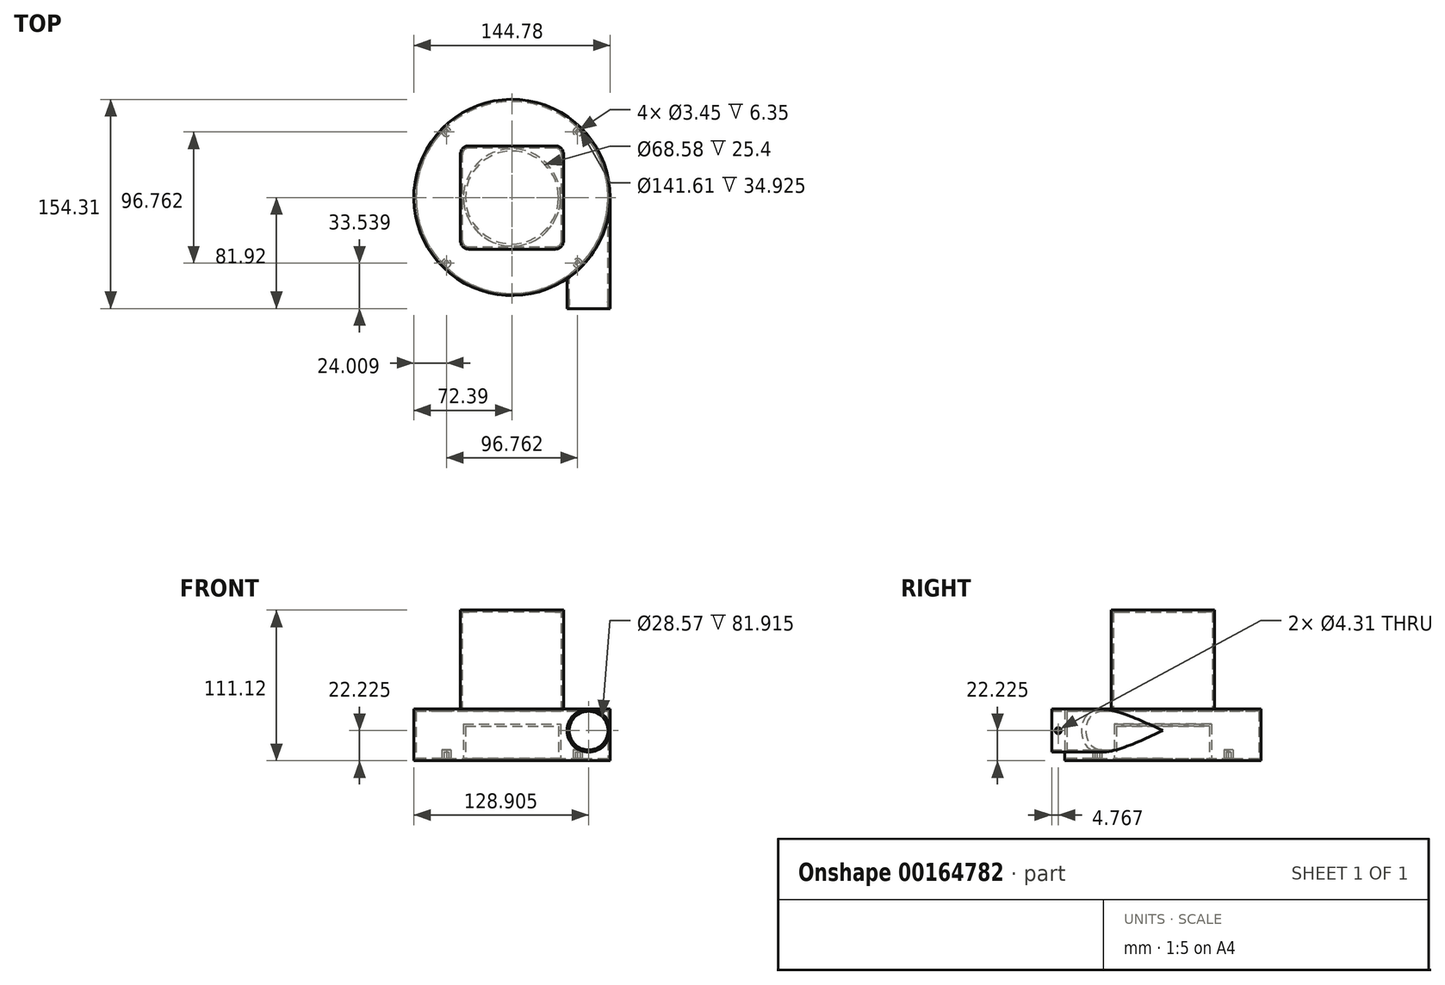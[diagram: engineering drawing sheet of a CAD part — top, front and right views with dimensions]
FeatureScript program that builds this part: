
annotation { "Feature Type Name" : "Feature", "Feature Type Description" : "" }
export const myFeature = defineFeature(function(context is Context, id is Id, definition is map)
    precondition{}
    {
        {
            var Q0;
            Q0=qCreatedBy(makeId("Top.planeOp"),FACE);
            var sketch = newSketch(context, id + "F0", { "sketchPlane" : qUnion([Q0])});
            skCircle(sketch, "E0", {"center": v(0, 0) * mm, "radius": 72.4 * mm});
            skSolve(sketch);
        }
        {
            var Q0;
            Q0=qSketchRegion(id+"F0",true);
            extrude(context, id + "F1", {"entities" : qUnion([Q0]), "depth" : 38.1 * mm});
        }
        {
            var Q0;
            Q0=makeQuery(id+"F1.opExtrude","CAP_FACE",FACE,{"disambiguationData":[OSD([sQuery(id+"F0.wireOp",EDGE,"E0")])],"isStart":false});
            var sketch = newSketch(context, id + "F2", { "sketchPlane" : qUnion([Q0])});
            skLineSegment(sketch, "E1.bottom", {"start": v(38.1, -38.1) * mm, "end": v(-38.1, -38.1) * mm});
            skLineSegment(sketch, "E1.top", {"start": v(38.1, 38.1) * mm, "end": v(-38.1, 38.1) * mm});
            skLineSegment(sketch, "E1.left", {"start": v(38.1, -38.1) * mm, "end": v(38.1, 38.1) * mm});
            skLineSegment(sketch, "E1.right", {"start": v(-38.1, -38.1) * mm, "end": v(-38.1, 38.1) * mm});
            skPoint(sketch, "E1.middle", {"position": v(0, 0) * mm});
            skSolve(sketch);
        }
        {
            var Q0;
            Q0=qSketchRegion(id+"F2",true);
            extrude(context, id + "F3", {"entities" : qUnion([Q0]), "operationType" : NewBodyOperationType.ADD, "depth" : 73.02 * mm});
        }
        {
            var Q0;
            Q0=makeQuery(id+"F3.opExtrude","SWEPT_EDGE",EDGE,{"disambiguationData":[OSD([sQuery(id+"F2.wireOp",EDGE,"E1.bottom"),sQuery(id+"F2.wireOp",EDGE,"E1.right")])]});
            var Q1;
            Q1=makeQuery(id+"F3.opExtrude","SWEPT_EDGE",EDGE,{"disambiguationData":[OSD([sQuery(id+"F2.wireOp",EDGE,"E1.top"),sQuery(id+"F2.wireOp",EDGE,"E1.right")])]});
            var Q2;
            Q2=makeQuery(id+"F3.opExtrude","SWEPT_EDGE",EDGE,{"disambiguationData":[OSD([sQuery(id+"F2.wireOp",EDGE,"E1.bottom"),sQuery(id+"F2.wireOp",EDGE,"E1.left")])]});
            var Q3;
            Q3=makeQuery(id+"F3.opExtrude","SWEPT_EDGE",EDGE,{"disambiguationData":[OSD([sQuery(id+"F2.wireOp",EDGE,"E1.top"),sQuery(id+"F2.wireOp",EDGE,"E1.left")])]});
            fillet(context, id + "F4", {"entities" : qUnion([Q0, Q1, Q2, Q3]), "radius" : 6.35 * mm, "tangentPropagation" : true, "allowEdgeOverflow" : false});
        }
        {
            var Q0;
            Q0=makeQuery(id+"F1.opExtrude","CAP_FACE",FACE,{"disambiguationData":[OSD([sQuery(id+"F0.wireOp",EDGE,"E0")])],"isStart":true});
            var sketch = newSketch(context, id + "F5", { "sketchPlane" : qUnion([Q0])});
            skLineSegment(sketch, "E2.bottom", {"start": v(48.38, 48.38) * mm, "end": v(-48.38, 48.38) * mm, "construction": true});
            skLineSegment(sketch, "E2.top", {"start": v(48.38, -48.38) * mm, "end": v(-48.38, -48.38) * mm, "construction": true});
            skLineSegment(sketch, "E2.left", {"start": v(48.38, 48.38) * mm, "end": v(48.38, -48.38) * mm, "construction": true});
            skLineSegment(sketch, "E2.right", {"start": v(-48.38, 48.38) * mm, "end": v(-48.38, -48.38) * mm, "construction": true});
            skPoint(sketch, "E2.middle", {"position": v(0, 0) * mm});
            skCircle(sketch, "E3", {"center": v(48.38, 48.38) * mm, "radius": 3.97 * mm, "construction": true});
            skCircle(sketch, "E4", {"center": v(-48.38, 48.38) * mm, "radius": 1.73 * mm});
            skCircle(sketch, "E5", {"center": v(-48.38, -48.38) * mm, "radius": 1.73 * mm});
            skCircle(sketch, "E6", {"center": v(48.38, -48.38) * mm, "radius": 1.73 * mm});
            skCircle(sketch, "E7", {"center": v(48.38, 48.38) * mm, "radius": 1.73 * mm});
            skSolve(sketch);
        }
        {
            var Q0;
            Q0=qSketchRegion(id+"F5",true);
            extrude(context, id + "F6", {"entities" : qUnion([Q0]), "operationType" : NewBodyOperationType.REMOVE, "oppositeDirection" : true, "depth" : 6.35 * mm});
        }
        {
            var Q0;
            Q0=makeQuery(id+"F1.opExtrude","CAP_FACE",FACE,{"disambiguationData":[OSD([sQuery(id+"F0.wireOp",EDGE,"E0")])],"isStart":true});
            var sketch = newSketch(context, id + "F7", { "sketchPlane" : qUnion([Q0])});
            skCircle(sketch, "E8", {"center": v(0, 0) * mm, "radius": 34.3 * mm});
            skSolve(sketch);
        }
        {
            var Q0;
            Q0=qSketchRegion(id+"F7",true);
            extrude(context, id + "F8", {"entities" : qUnion([Q0]), "operationType" : NewBodyOperationType.REMOVE, "oppositeDirection" : true, "depth" : 25.4 * mm});
        }
        {
            var Q0;
            Q0=qCreatedBy(makeId("Front.planeOp"),FACE);
            var sketch = newSketch(context, id + "F9", { "sketchPlane" : qUnion([Q0])});
            skCircle(sketch, "E9", {"center": v(56.52, 22.23) * mm, "radius": 15.88 * mm});
            skLineSegment(sketch, "E10.bottom", {"start": v(0, 0) * mm, "end": v(72.4, 0) * mm, "construction": true});
            skLineSegment(sketch, "E10.top", {"start": v(0, 38.1) * mm, "end": v(72.4, 38.1) * mm, "construction": true});
            skLineSegment(sketch, "E10.left", {"start": v(0, 0) * mm, "end": v(0, 38.1) * mm, "construction": true});
            skLineSegment(sketch, "E10.right", {"start": v(72.4, 0) * mm, "end": v(72.4, 38.1) * mm, "construction": true});
            skSolve(sketch);
        }
        {
            var Q0;
            Q0 = qSketchRegion(id + "F9", true);
            extrude(context, id + "F10", {"entities" : qUnion([Q0]), "operationType" : NewBodyOperationType.ADD, "depth" : 81.9 * mm});
        }
        {
            var Q0;
            Q0=makeQuery(id+"F10.opExtrude","CAP_FACE",FACE,{"disambiguationData":[OSD([sQuery(id+"F9.wireOp",EDGE,"E9")])],"isStart":false});
            shell(context, id + "F11", {"entities" : qUnion([Q0]), "thickness" : 1.59 * mm});
        }
        {
            var Q0;
            Q0=qCreatedBy(makeId("Right.planeOp"),FACE);
            var sketch = newSketch(context, id + "F12", { "sketchPlane" : qUnion([Q0])});
            skLineSegment(sketch, "E11", {"start": v(-81.92, 22.23) * mm, "end": v(-77.15, 22.23) * mm, "construction": true});
            skCircle(sketch, "E12", {"center": v(-77.15, 22.23) * mm, "radius": 2.15 * mm});
            skSolve(sketch);
        }
        {
            var Q0;
            Q0 = qSketchRegion(id + "F12", true);
            var Q1;
            Q1=makeQuery(id+"F10.opExtrude","SWEPT_FACE",FACE,{"disambiguationData":[OSD([sQuery(id+"F9.wireOp",EDGE,"E9")])]});
            extrude(context, id + "F13", {"entities" : qUnion([Q0]), "operationType" : NewBodyOperationType.REMOVE, "endBound" : BoundingType.THROUGH_ALL, "endBoundEntityFace" : qUnion([Q1]), "depth" : 25.4 * mm});
        }
    });
